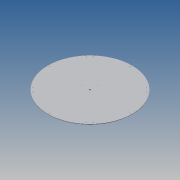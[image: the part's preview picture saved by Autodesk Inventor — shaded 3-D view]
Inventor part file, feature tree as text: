
AUTODESK INVENTOR PART (.ipt)
format: ipt  version: 2014 SP1 (Build 180222100, 222)  size: 185,344 bytes
history: native  units: in
note: dims shown in document units (in); Inventor stores cm internally (conversion verified against a paired STEP export)
features: sketch x5, hole x3, pattern_circular x3, extrude x2
ambient origin geometry x8: Origin, YZ Plane, XZ Plane, XY Plane, X Axis, Y Axis, Z Axis, Center Point
bodies: Body1 (feature_tree)
feature tree (13):
  extrude  "Extrusion1"  Depth=0.125in TaperAngle=0.0deg
  extrude  "Extrusion2"  Depth=0.125in TaperAngle=0.0deg
  hole  "Hole1"  [1 undecoded]
  pattern_circular  "Circular Pattern1"  Angle=45.0deg  [1 undecoded]
  hole  "Hole2"  [1 undecoded]
  pattern_circular  "Circular Pattern2"  [2 undecoded]
  hole  "Hole5"  [1 undecoded]
  pattern_circular  "Circular Pattern5"  [2 undecoded]
  sketch  "Sketch1"  dims[d0=24.0in d1=0.125in d2=0.0in]
  sketch  "Sketch2"  dims[d3=0.5in d4=0.125in d5=0.0in]
  sketch  "Sketch3"  dims[d6=11.5in]
  sketch  "Sketch4"  dims[d7=0.177in d8=0.2362in d9=0.332in d10=0.0787in d11=0.5635in d12=0.315in d13=0.8108in d14=1.5748in d15=360.0deg]
  sketch  "Sketch7"  dims[d20=11.5in d21=45.0deg d22=0.719in d23=0.719in d24=0.177in d25=0.2362in d26=0.332in d27=0.0787in d28=0.5635in d29=0.315in d30=0.8108in d31=1.5748in d32=360.0deg d60=2.25in d61=0.1495in d62=0.2362in d63=0.279in d64=0.0787in d65=0.5635in d66=0.315in d67=0.8108in d68=1.5748in d69=360.0deg]
note: 8 required parameter values undecoded (feature->parameter linkage not recoverable at this tier; creation-order binding heuristic only, values carry confidence <= 0.55)
